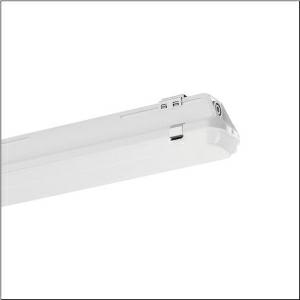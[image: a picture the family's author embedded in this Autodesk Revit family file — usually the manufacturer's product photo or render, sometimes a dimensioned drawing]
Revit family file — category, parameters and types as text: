
# Revit family: monsun_21_emergency_51fb10dp467c3h
name_source: partatom
category: Lighting Fixtures
units: mm (PartAtom-declared; Revit-internal decimal feet)

## family parameters
Cut with Voids When Loaded = No
Host = Face
Light Source = No
Part Type = Normal
Room Calculation Point = No
Round Connector Dimension = Use Diameter
Shared = No

## types (1)
- --- (1 x LED, 6060 lm, 36.5 W, 4000K)
    Apparent Load = 37 VA
    CIE Flux Codes = 47 77 93 94 100
    Color Rendering = 80
    Color Temperature = 4000K
    Default Elevation = 1800 mm
    Description = Monsun 21 emergency, damp-proof luminaire, chain hanger, primary optical cover: enclosure, of PMMA, light emission: direct distribution, primary light characteristic: symmetric, installation type: vertical mounting, horizontal mounting, surface-mounted, suspended mounting, LED, rated luminous flux: 6.060lm, luminous efficacy: 185lm/W, light colour: 840, colour temperature: 4000K, control gear: DALI 2, with terminal, 5+3-pole, max. 2.5mm², mains connection: 220..240V, AC, 50/60Hz, rated input power: 37W, control gear: single battery element, battery: LiFePO4, 9Ah, housing, of glass-fibre reinforced polyester, uncoated, bright grey, incl. chain hanger, length: 1.590mm, width: 90mm, height: 88mm, clip for enclosure, of stainless steel (V2A), ceiling mounting element, of stainless steel (V2A), chain hanger, of stainless steel (V2A), protection rating (complete): IP66, insulation class (complete): insulation class I (protective earthing), certification: CE, UKCA, protection symbol: D, impact resistance: IK04, permissible operating ambient temperature: +5..+25°C, standard: EN 50419, EN 60598-2-1, EN 60598-2-22, corresponds to IFS (International Featured Standards) requirements for safety and quality in the food industry, for indoor or canopied outdoor use, no direct snow, no direct sun, no direct rain, LABS conformity tested according to VDMA 24364:2018-05, contact your sales advisor before using the luminaires in applications with unclear chemical exposure, large temperature fluctuations or condensation-forming humidity, packaging unit: 1 piece
    Height = 89 mm
    Lamp = 1 x LED
    Lamp Light Flux = 6060 lm
    Lamp Power = 36.5 W
    Lamp count = 1
    Length = 1590 mm
    Luminous efficacy = 166 lm/W
    Manufacturer = Siteco
    ModVariant = No
    Model = 51FB10DP467C3H
    Mounting Place = Ceiling
    Mounting Type = Surface mounted
    Number of Poles = 1
    OnlyDefault = Yes
    Power Factor = 1
    Product Name = Monsun 21 emergency
    Product group = damp-proof luminaire
    ProductGroupID = 300
    Protection Class = Protection class I
    Protection Degree = IP 66
    RLX_Detail_Level = 1
    RLX_Emergency_Light_Flux = 0 lm
    RLX_Emergency_Type = 0
    RLX_Emergency_Type_DB = No
    RlxData = <blob elided: 92421 chars, md5=e30fd569>
    Socket = socket
    Standby Power = 0 W
    System Light Flux = 6060 lm
    System Power = 37 W
    Type Comments = : luminous flux: 100 % | dim-lin: 254 | 229 mA
    Type Image = l_1319656.jpg
    URL = http://relux.com
    VarID = @adj_038237
    Voltage = 0 V
    Weight = 0.00 kg
    Width = 90 mm

## geometry (parser evidence)
native form markers: Blend x4, Sweep x12
no freeform markers — native parametric forms only
